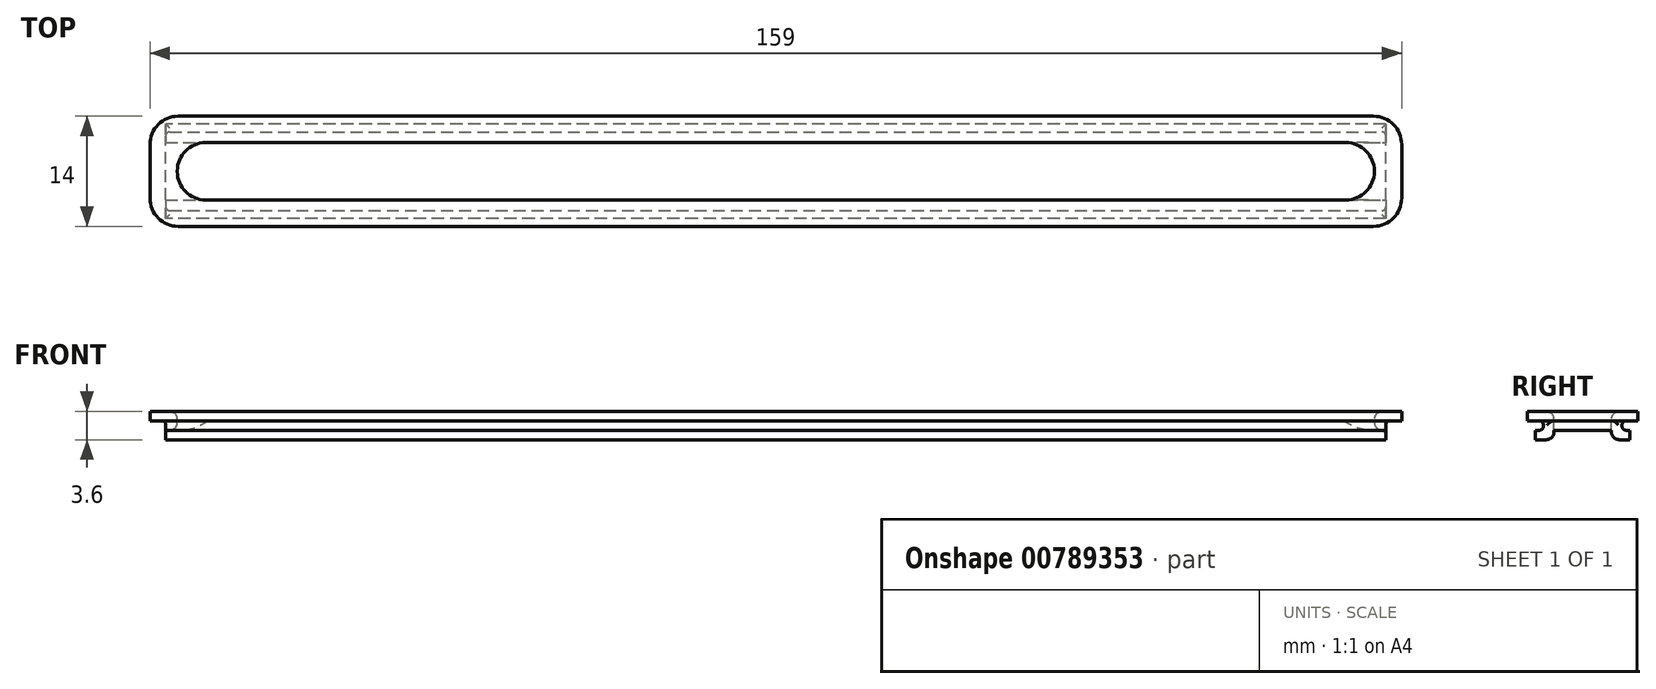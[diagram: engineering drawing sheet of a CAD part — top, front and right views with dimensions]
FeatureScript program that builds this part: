
annotation { "Feature Type Name" : "Feature", "Feature Type Description" : "" }
export const myFeature = defineFeature(function(context is Context, id is Id, definition is map)
    precondition{}
    {
        {
            var Q0;
            Q0=qCreatedBy(makeId("Top.planeOp"),FACE);
            var sketch = newSketch(context, id + "F0", { "sketchPlane" : qUnion([Q0])});
            skLineSegment(sketch, "E0.bottom", {"start": v(0, 0) * mm, "end": v(155, 0) * mm});
            skLineSegment(sketch, "E0.top", {"start": v(0, 10) * mm, "end": v(155, 10) * mm});
            skLineSegment(sketch, "E0.left", {"start": v(0, 0) * mm, "end": v(0, 10) * mm});
            skLineSegment(sketch, "E0.right", {"start": v(155, 0) * mm, "end": v(155, 10) * mm});
            skLineSegment(sketch, "E1.bottom", {"start": v(1.47, 8.64) * mm, "end": v(153.53, 8.64) * mm});
            skLineSegment(sketch, "E1.top", {"start": v(1.47, 1.36) * mm, "end": v(153.53, 1.36) * mm});
            skLineSegment(sketch, "E1.left", {"start": v(1.47, 8.64) * mm, "end": v(1.47, 1.36) * mm});
            skLineSegment(sketch, "E1.right", {"start": v(153.53, 8.64) * mm, "end": v(153.53, 1.36) * mm});
            skSolve(sketch);
        }
        {
            var Q0;
            Q0 = qSketchRegion(id + "F0", true);
            extrude(context, id + "F1", {"entities" : qUnion([Q0]), "depth" : 1.2 * mm, "offsetDistance" : 25 * mm});
        }
        {
            var Q0;
            Q0=makeQuery(id+"F1.opExtrude","CAP_FACE",FACE,{"disambiguationData":[OSD([sQuery(id+"F0.wireOp",EDGE,"E0.bottom"),sQuery(id+"F0.wireOp",EDGE,"E0.top"),sQuery(id+"F0.wireOp",EDGE,"E0.left"),sQuery(id+"F0.wireOp",EDGE,"E0.right"),sQuery(id+"F0.wireOp",EDGE,"E1.bottom"),sQuery(id+"F0.wireOp",EDGE,"E1.top"),sQuery(id+"F0.wireOp",EDGE,"E1.left"),sQuery(id+"F0.wireOp",EDGE,"E1.right")])],"isStart":false});
            var sketch = newSketch(context, id + "F2", { "sketchPlane" : qUnion([Q0])});
            skLineSegment(sketch, "E2.bottom", {"start": v(157, 12) * mm, "end": v(-2, 12) * mm});
            skLineSegment(sketch, "E2.top", {"start": v(157, -2) * mm, "end": v(-2, -2) * mm});
            skLineSegment(sketch, "E2.left", {"start": v(157, 12) * mm, "end": v(157, -2) * mm});
            skLineSegment(sketch, "E2.right", {"start": v(-2, 12) * mm, "end": v(-2, -2) * mm});
            skPoint(sketch, "E2.middle", {"position": v(77.5, 5) * mm});
            skPoint(sketch, "E2.middle.positionSnap0", {"position": v(77.5, 1.36) * mm});
            skPoint(sketch, "E2.middle.positionSnap1", {"position": v(1.47, 5) * mm});
            skPoint(sketch, "E2.centerSnap0", {"position": v(77.5, 1.36) * mm});
            skPoint(sketch, "E2.centerSnap1", {"position": v(1.47, 5) * mm});
            skSolve(sketch);
        }
        {
            var Q0;
            {var subQ0=sQuery(id+"F2.wireOp",EDGE,"E2.bottom");Q0=makeQuery(id+"F2.imprint","IMPRINT",FACE,{"disambiguationData":[TD([[makeQuery(id+"F2.imprint","IMPRINT",EDGE,{"derivedFrom":subQ0}),1.0]])]});}
            var Q1;
            {var subQ0=sQuery(id+"F2.wireOp",EDGE,"E2.top");Q1=makeQuery(id+"F2.imprint","IMPRINT",FACE,{"disambiguationData":[TD([[makeQuery(id+"F2.imprint","IMPRINT",EDGE,{"derivedFrom":subQ0}),-1.0]])]});}
            var Q2;
            {var subQ2=makeQuery(id+"F1.opExtrude","CAP_EDGE",EDGE,{"disambiguationData":[OSD([sQuery(id+"F0.wireOp",EDGE,"E0.bottom")])],"isStart":false});Q2=makeQuery(id+"F2.imprint","IMPRINT",FACE,{"disambiguationData":[TD([[makeQuery(id+"F2.imprint","IMPRINT",EDGE,{"derivedFrom":subQ2}),1.0]])]});}
            extrude(context, id + "F3", {"entities" : qUnion([Q0, Q1, Q2]), "operationType" : NewBodyOperationType.ADD, "depth" : 1.2 * mm, "offsetDistance" : 25 * mm});
        }
        {
            var Q0;
            Q0=makeQuery(id+"F1.opExtrude","CAP_FACE",FACE,{"disambiguationData":[OSD([sQuery(id+"F0.wireOp",EDGE,"E0.bottom"),sQuery(id+"F0.wireOp",EDGE,"E0.top"),sQuery(id+"F0.wireOp",EDGE,"E0.left"),sQuery(id+"F0.wireOp",EDGE,"E0.right"),sQuery(id+"F0.wireOp",EDGE,"E1.bottom"),sQuery(id+"F0.wireOp",EDGE,"E1.top"),sQuery(id+"F0.wireOp",EDGE,"E1.left"),sQuery(id+"F0.wireOp",EDGE,"E1.right")])],"isStart":true});
            var sketch = newSketch(context, id + "F4", { "sketchPlane" : qUnion([Q0])});
            skLineSegment(sketch, "E3.bottom", {"start": v(155, 1) * mm, "end": v(0, 1) * mm});
            skLineSegment(sketch, "E3.top", {"start": v(155, -11) * mm, "end": v(0, -11) * mm});
            skLineSegment(sketch, "E3.left", {"start": v(155, 1) * mm, "end": v(155, -11) * mm});
            skLineSegment(sketch, "E3.right", {"start": v(0, 1) * mm, "end": v(0, -11) * mm});
            skPoint(sketch, "E3.middle", {"position": v(77.5, -5) * mm});
            skPoint(sketch, "E3.middle.positionSnap0", {"position": v(0, -5) * mm});
            skPoint(sketch, "E3.middle.positionSnap1", {"position": v(77.5, -8.64) * mm});
            skPoint(sketch, "E3.centerSnap0", {"position": v(0, -5) * mm});
            skPoint(sketch, "E3.centerSnap1", {"position": v(77.5, -8.64) * mm});
            skLineSegment(sketch, "E4", {"start": v(0, -1.36) * mm, "end": v(155, -1.36) * mm});
            skLineSegment(sketch, "E5", {"start": v(0, -8.64) * mm, "end": v(155, -8.64) * mm});
            skSolve(sketch);
        }
        {
            var Q0;
            {var subQ0=sQuery(id+"F4.wireOp",EDGE,"E3.bottom");Q0=makeQuery(id+"F4.imprint","IMPRINT",FACE,{"disambiguationData":[TD([[makeQuery(id+"F4.imprint","IMPRINT",EDGE,{"derivedFrom":subQ0}),1.0]])]});}
            var Q1;
            {var subQ5=makeQuery(id+"F1.opExtrude","CAP_EDGE",EDGE,{"disambiguationData":[OSD([sQuery(id+"F0.wireOp",EDGE,"E0.bottom")])],"isStart":true});Q1=makeQuery(id+"F4.imprint","IMPRINT",FACE,{"disambiguationData":[TD([[makeQuery(id+"F4.imprint","IMPRINT",EDGE,{"derivedFrom":subQ5}),-1.0]])]});}
            var Q2;
            {var subQ4=makeQuery(id+"F1.opExtrude","CAP_EDGE",EDGE,{"disambiguationData":[OSD([sQuery(id+"F0.wireOp",EDGE,"E0.top")])],"isStart":true});Q2=makeQuery(id+"F4.imprint","IMPRINT",FACE,{"disambiguationData":[TD([[makeQuery(id+"F4.imprint","IMPRINT",EDGE,{"derivedFrom":subQ4}),1.0]])]});}
            var Q3;
            {var subQ0=sQuery(id+"F4.wireOp",EDGE,"E3.top");Q3=makeQuery(id+"F4.imprint","IMPRINT",FACE,{"disambiguationData":[TD([[makeQuery(id+"F4.imprint","IMPRINT",EDGE,{"derivedFrom":subQ0}),-1.0]])]});}
            extrude(context, id + "F5", {"entities" : qUnion([Q0, Q1, Q2, Q3]), "operationType" : NewBodyOperationType.ADD, "depth" : 1.2 * mm, "offsetDistance" : 25 * mm});
        }
        {
            var Q0;
            {var subQ0=sQuery(id+"F0.wireOp",EDGE,"E1.left");var subQ1=sQuery(id+"F0.wireOp",EDGE,"E1.top");Q0=makeQuery(id+"F3.boolean.opBoolean","MERGE",EDGE,{"derivedFrom":[makeQuery(id+"F1.opExtrude","SWEPT_EDGE",EDGE,{"disambiguationData":[OSD([subQ1,subQ0])]}),makeQuery(id+"F3.opExtrude","SWEPT_EDGE",EDGE,{"disambiguationData":[OSD([subQ1,subQ0])]})]});}
            var Q1;
            {var subQ0=sQuery(id+"F0.wireOp",EDGE,"E1.left");var subQ1=sQuery(id+"F0.wireOp",EDGE,"E1.bottom");Q1=makeQuery(id+"F3.boolean.opBoolean","MERGE",EDGE,{"derivedFrom":[makeQuery(id+"F1.opExtrude","SWEPT_EDGE",EDGE,{"disambiguationData":[OSD([subQ1,subQ0])]}),makeQuery(id+"F3.opExtrude","SWEPT_EDGE",EDGE,{"disambiguationData":[OSD([subQ1,subQ0])]})]});}
            var Q2;
            {var subQ0=sQuery(id+"F0.wireOp",EDGE,"E1.right");var subQ1=sQuery(id+"F0.wireOp",EDGE,"E1.top");Q2=makeQuery(id+"F3.boolean.opBoolean","MERGE",EDGE,{"derivedFrom":[makeQuery(id+"F1.opExtrude","SWEPT_EDGE",EDGE,{"disambiguationData":[OSD([subQ1,subQ0])]}),makeQuery(id+"F3.opExtrude","SWEPT_EDGE",EDGE,{"disambiguationData":[OSD([subQ1,subQ0])]})]});}
            var Q3;
            {var subQ0=sQuery(id+"F0.wireOp",EDGE,"E1.right");var subQ1=sQuery(id+"F0.wireOp",EDGE,"E1.bottom");Q3=makeQuery(id+"F3.boolean.opBoolean","MERGE",EDGE,{"derivedFrom":[makeQuery(id+"F1.opExtrude","SWEPT_EDGE",EDGE,{"disambiguationData":[OSD([subQ1,subQ0])]}),makeQuery(id+"F3.opExtrude","SWEPT_EDGE",EDGE,{"disambiguationData":[OSD([subQ1,subQ0])]})]});}
            var Q4;
            Q4=makeQuery(id+"F3.opExtrude","SWEPT_EDGE",EDGE,{"disambiguationData":[OSD([sQuery(id+"F2.wireOp",EDGE,"E2.top"),sQuery(id+"F2.wireOp",EDGE,"E2.left")])]});
            var Q5;
            Q5=makeQuery(id+"F3.opExtrude","SWEPT_EDGE",EDGE,{"disambiguationData":[OSD([sQuery(id+"F2.wireOp",EDGE,"E2.bottom"),sQuery(id+"F2.wireOp",EDGE,"E2.left")])]});
            var Q6;
            Q6=makeQuery(id+"F3.opExtrude","SWEPT_EDGE",EDGE,{"disambiguationData":[OSD([sQuery(id+"F2.wireOp",EDGE,"E2.bottom"),sQuery(id+"F2.wireOp",EDGE,"E2.right")])]});
            var Q7;
            Q7=makeQuery(id+"F3.opExtrude","SWEPT_EDGE",EDGE,{"disambiguationData":[OSD([sQuery(id+"F2.wireOp",EDGE,"E2.top"),sQuery(id+"F2.wireOp",EDGE,"E2.right")])]});
            fillet(context, id + "F6", {"entities" : qUnion([Q0, Q1, Q2, Q3, Q4, Q5, Q6, Q7]), "radius" : 3.6 * mm, "allowEdgeOverflow" : false});
        }
        {
            var Q0;
            {var subQ1=sQuery(id+"F0.wireOp",EDGE,"E0.bottom");var subQ4=sQuery(id+"F0.wireOp",EDGE,"E1.left");var subQ5=sQuery(id+"F0.wireOp",EDGE,"E0.top");var subQ8=sQuery(id+"F0.wireOp",EDGE,"E0.left");var subQ9=sQuery(id+"F0.wireOp",EDGE,"E1.bottom");var subQ10=sQuery(id+"F0.wireOp",EDGE,"E1.top");Q0=makeQuery(id+"F6.opFillet","BLEND_EDGE",EDGE,{"blendedFrom":[makeQuery(id+"F3.boolean.opBoolean","MERGE",EDGE,{"derivedFrom":[makeQuery(id+"F1.opExtrude","SWEPT_EDGE",EDGE,{"disambiguationData":[OSD([subQ9,subQ4])]}),makeQuery(id+"F3.opExtrude","SWEPT_EDGE",EDGE,{"disambiguationData":[OSD([subQ9,subQ4])]})]}),makeQuery(id+"F5.boolean.opBoolean","SPLIT",FACE,{"disambiguationData":[TD([makeQuery(id+"F1.opExtrude","SWEPT_FACE",FACE,{"disambiguationData":[OSD([subQ8])]})])],"derivedFrom":makeQuery(id+"F1.opExtrude","CAP_FACE",FACE,{"disambiguationData":[OSD([subQ1,subQ5,subQ8,sQuery(id+"F0.wireOp",EDGE,"E0.right"),subQ9,subQ10,subQ4,sQuery(id+"F0.wireOp",EDGE,"E1.right")])],"isStart":true})})],"blendedInto":[makeQuery(id+"F5.boolean.opBoolean","SPLIT",FACE,{"disambiguationData":[TD([makeQuery(id+"F1.opExtrude","SWEPT_FACE",FACE,{"disambiguationData":[OSD([subQ8])]})])],"derivedFrom":makeQuery(id+"F1.opExtrude","CAP_FACE",FACE,{"disambiguationData":[OSD([subQ1,subQ5,subQ8,sQuery(id+"F0.wireOp",EDGE,"E0.right"),subQ9,subQ10,subQ4,sQuery(id+"F0.wireOp",EDGE,"E1.right")])],"isStart":true})})]});}
            var Q1;
            {var subQ0=sQuery(id+"F0.wireOp",EDGE,"E1.left");var subQ1=sQuery(id+"F0.wireOp",EDGE,"E1.bottom");Q1=makeQuery(id+"F6.opFillet","BLEND_EDGE",EDGE,{"blendedFrom":[makeQuery(id+"F3.boolean.opBoolean","MERGE",EDGE,{"derivedFrom":[makeQuery(id+"F1.opExtrude","SWEPT_EDGE",EDGE,{"disambiguationData":[OSD([subQ1,subQ0])]}),makeQuery(id+"F3.opExtrude","SWEPT_EDGE",EDGE,{"disambiguationData":[OSD([subQ1,subQ0])]})]}),makeQuery(id+"F3.opExtrude","CAP_FACE",FACE,{"disambiguationData":[OSD([subQ1,sQuery(id+"F0.wireOp",EDGE,"E1.top"),subQ0,sQuery(id+"F0.wireOp",EDGE,"E1.right"),sQuery(id+"F2.wireOp",EDGE,"E2.bottom"),sQuery(id+"F2.wireOp",EDGE,"E2.top"),sQuery(id+"F2.wireOp",EDGE,"E2.left"),sQuery(id+"F2.wireOp",EDGE,"E2.right")])],"isStart":false})],"blendedInto":[makeQuery(id+"F3.opExtrude","CAP_FACE",FACE,{"disambiguationData":[OSD([subQ1,sQuery(id+"F0.wireOp",EDGE,"E1.top"),subQ0,sQuery(id+"F0.wireOp",EDGE,"E1.right"),sQuery(id+"F2.wireOp",EDGE,"E2.bottom"),sQuery(id+"F2.wireOp",EDGE,"E2.top"),sQuery(id+"F2.wireOp",EDGE,"E2.left"),sQuery(id+"F2.wireOp",EDGE,"E2.right")])],"isStart":false})]});}
            var Q2;
            {var subQ1=sQuery(id+"F0.wireOp",EDGE,"E0.top");var subQ4=sQuery(id+"F0.wireOp",EDGE,"E0.bottom");var subQ7=sQuery(id+"F0.wireOp",EDGE,"E1.right");var subQ8=sQuery(id+"F0.wireOp",EDGE,"E1.top");var subQ9=sQuery(id+"F0.wireOp",EDGE,"E0.right");var subQ10=sQuery(id+"F0.wireOp",EDGE,"E1.bottom");Q2=makeQuery(id+"F6.opFillet","BLEND_EDGE",EDGE,{"blendedFrom":[makeQuery(id+"F3.boolean.opBoolean","MERGE",EDGE,{"derivedFrom":[makeQuery(id+"F1.opExtrude","SWEPT_EDGE",EDGE,{"disambiguationData":[OSD([subQ10,subQ7])]}),makeQuery(id+"F3.opExtrude","SWEPT_EDGE",EDGE,{"disambiguationData":[OSD([subQ10,subQ7])]})]}),makeQuery(id+"F5.boolean.opBoolean","SPLIT",FACE,{"disambiguationData":[TD([makeQuery(id+"F1.opExtrude","SWEPT_FACE",FACE,{"disambiguationData":[OSD([subQ9])]})])],"derivedFrom":makeQuery(id+"F1.opExtrude","CAP_FACE",FACE,{"disambiguationData":[OSD([subQ4,subQ1,sQuery(id+"F0.wireOp",EDGE,"E0.left"),subQ9,subQ10,subQ8,sQuery(id+"F0.wireOp",EDGE,"E1.left"),subQ7])],"isStart":true})})],"blendedInto":[makeQuery(id+"F5.boolean.opBoolean","SPLIT",FACE,{"disambiguationData":[TD([makeQuery(id+"F1.opExtrude","SWEPT_FACE",FACE,{"disambiguationData":[OSD([subQ9])]})])],"derivedFrom":makeQuery(id+"F1.opExtrude","CAP_FACE",FACE,{"disambiguationData":[OSD([subQ4,subQ1,sQuery(id+"F0.wireOp",EDGE,"E0.left"),subQ9,subQ10,subQ8,sQuery(id+"F0.wireOp",EDGE,"E1.left"),subQ7])],"isStart":true})})]});}
            var Q3;
            Q3=makeQuery(id+"F5.opExtrude","CAP_EDGE",EDGE,{"disambiguationData":[OSD([sQuery(id+"F4.wireOp",EDGE,"E4")])],"isStart":false});
            var Q4;
            Q4=makeQuery(id+"F5.opExtrude","CAP_EDGE",EDGE,{"disambiguationData":[OSD([sQuery(id+"F4.wireOp",EDGE,"E5")])],"isStart":false});
            fillet(context, id + "F7", {"entities" : qUnion([Q0, Q1, Q2, Q3, Q4]), "radius" : 1 * mm, "tangentPropagation" : true, "allowEdgeOverflow" : false});
        }
        {
            var Q0;
            Q0=makeQuery(id+"F1.opExtrude","SWEPT_FACE",FACE,{"disambiguationData":[OSD([sQuery(id+"F0.wireOp",EDGE,"E0.bottom")])]});
            var Q1;
            Q1=makeQuery(id+"F1.opExtrude","SWEPT_FACE",FACE,{"disambiguationData":[OSD([sQuery(id+"F0.wireOp",EDGE,"E0.top")])]});
            fillet(context, id + "F8", {"entities" : qUnion([Q0, Q1]), "radius" : 0.5 * mm, "tangentPropagation" : true, "allowEdgeOverflow" : false});
        }
    });
